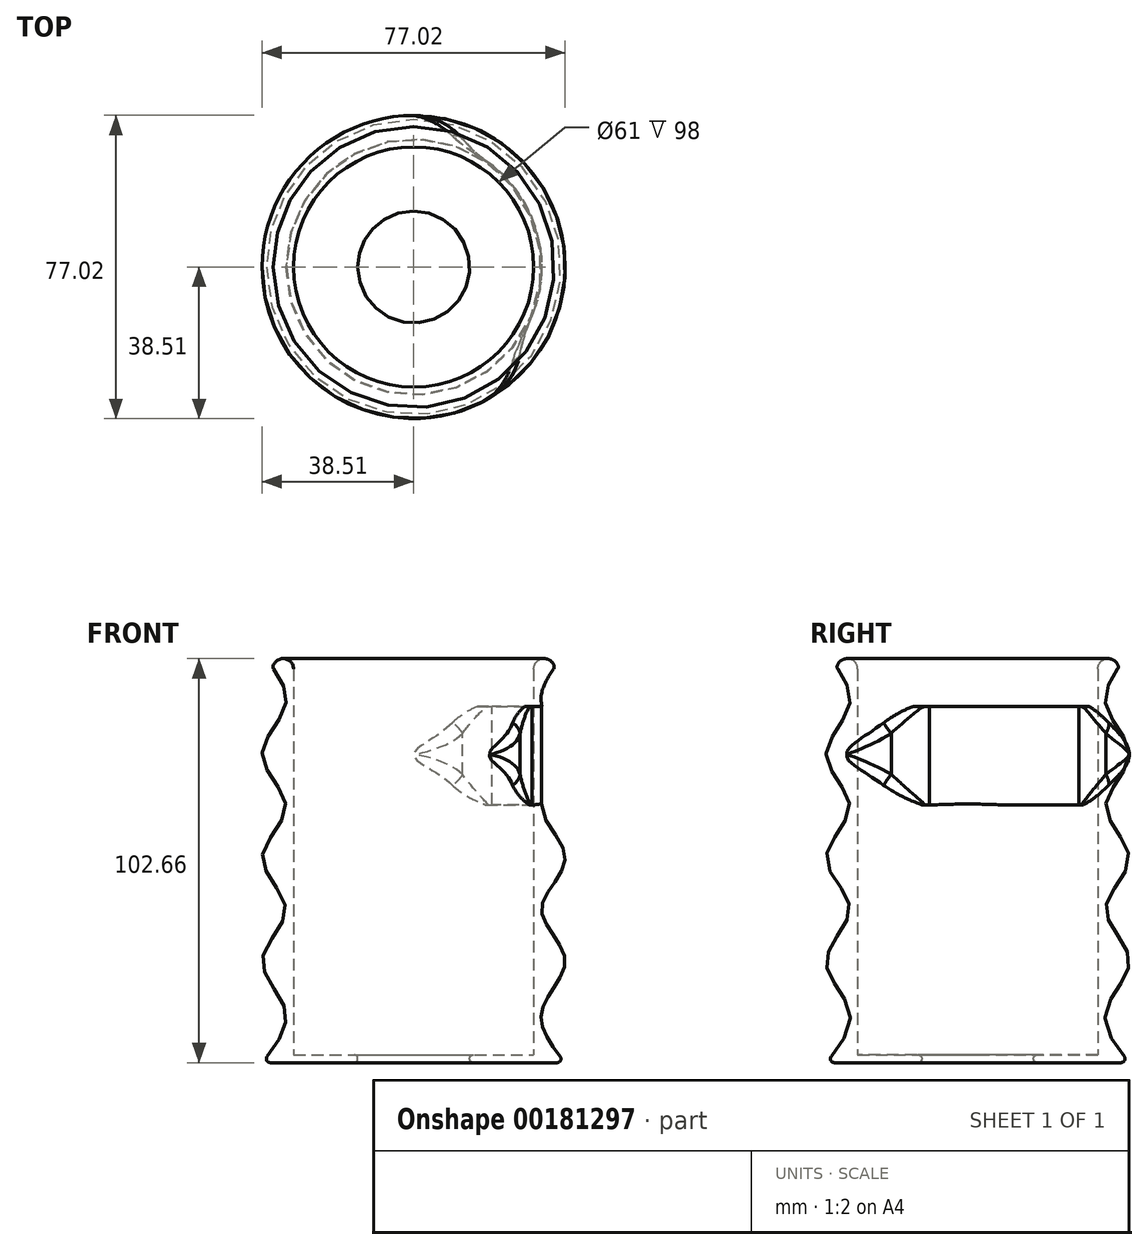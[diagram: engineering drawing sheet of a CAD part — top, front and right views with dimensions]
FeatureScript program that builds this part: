
annotation { "Feature Type Name" : "Feature", "Feature Type Description" : "" }
export const myFeature = defineFeature(function(context is Context, id is Id, definition is map)
    precondition{}
    {
        {
            var Q0;
            Q0=qCreatedBy(makeId("Front.planeOp"),FACE);
            var sketch = newSketch(context, id + "F0", { "sketchPlane" : qUnion([Q0])});
            skLineSegment(sketch, "E0", {"start": v(30.5, 0) * mm, "end": v(30.5, 100) * mm});
            skLineSegment(sketch, "E1", {"start": v(0, 13) * mm, "end": v(106.96, 13) * mm, "construction": true});
            skLineSegment(sketch, "E2.0.1.0", {"start": v(0, 26) * mm, "end": v(106.96, 26) * mm, "construction": true});
            skLineSegment(sketch, "E2.0.2.0", {"start": v(0, 39) * mm, "end": v(106.96, 39) * mm, "construction": true});
            skLineSegment(sketch, "E2.0.3.0", {"start": v(0, 52) * mm, "end": v(106.96, 52) * mm, "construction": true});
            skLineSegment(sketch, "E2.0.4.0", {"start": v(0, 65) * mm, "end": v(106.96, 65) * mm, "construction": true});
            skLineSegment(sketch, "E2.0.5.0", {"start": v(0, 78) * mm, "end": v(106.96, 78) * mm, "construction": true});
            skLineSegment(sketch, "E2.0.6.0", {"start": v(0, 91) * mm, "end": v(106.96, 91) * mm, "construction": true});
            skLineSegment(sketch, "E2.0.7.0", {"start": v(0, 104) * mm, "end": v(106.96, 104) * mm, "construction": true});
            skLineSegment(sketch, "E2.1.0.0", {"start": v(25, 13.02) * mm, "end": v(131.96, 13.02) * mm, "construction": true});
            skLineSegment(sketch, "E2.1.1.0", {"start": v(25, 26.02) * mm, "end": v(131.96, 26.02) * mm, "construction": true});
            skLineSegment(sketch, "E2.1.2.0", {"start": v(25, 39.02) * mm, "end": v(131.96, 39.02) * mm, "construction": true});
            skLineSegment(sketch, "E2.1.3.0", {"start": v(25, 52.02) * mm, "end": v(131.96, 52.02) * mm, "construction": true});
            skLineSegment(sketch, "E2.1.4.0", {"start": v(25, 65.02) * mm, "end": v(131.96, 65.02) * mm, "construction": true});
            skLineSegment(sketch, "E2.1.5.0", {"start": v(25, 78.02) * mm, "end": v(131.96, 78.02) * mm, "construction": true});
            skLineSegment(sketch, "E2.1.6.0", {"start": v(25, 91.02) * mm, "end": v(131.96, 91.02) * mm, "construction": true});
            skLineSegment(sketch, "E2.1.7.0", {"start": v(25, 104.02) * mm, "end": v(131.96, 104.02) * mm, "construction": true});
            skLineSegment(sketch, "E2.2.0.0", {"start": v(50, 13.04) * mm, "end": v(156.96, 13.04) * mm, "construction": true});
            skLineSegment(sketch, "E2.2.1.0", {"start": v(50, 26.04) * mm, "end": v(156.96, 26.04) * mm, "construction": true});
            skLineSegment(sketch, "E2.2.2.0", {"start": v(50, 39.04) * mm, "end": v(156.96, 39.04) * mm, "construction": true});
            skLineSegment(sketch, "E2.2.3.0", {"start": v(50, 52.04) * mm, "end": v(156.96, 52.04) * mm, "construction": true});
            skLineSegment(sketch, "E2.2.4.0", {"start": v(50, 65.04) * mm, "end": v(156.96, 65.04) * mm, "construction": true});
            skLineSegment(sketch, "E2.2.5.0", {"start": v(50, 78.04) * mm, "end": v(156.96, 78.04) * mm, "construction": true});
            skLineSegment(sketch, "E2.2.6.0", {"start": v(50, 91.04) * mm, "end": v(156.96, 91.04) * mm, "construction": true});
            skLineSegment(sketch, "E2.2.7.0", {"start": v(50, 104.04) * mm, "end": v(156.96, 104.04) * mm, "construction": true});
            skLineSegment(sketch, "E2.direction1", {"start": v(0, 13) * mm, "end": v(25, 13.02) * mm, "construction": true});
            skLineSegment(sketch, "E2.direction2", {"start": v(0, 13) * mm, "end": v(0, 26) * mm, "construction": true});
            skLineSegment(sketch, "E3", {"start": v(32.5, 0) * mm, "end": v(32.5, 104) * mm, "construction": true});
            skLineSegment(sketch, "E4", {"start": v(38.5, 0) * mm, "end": v(38.5, 104) * mm, "construction": true});
            skFitSpline(sketch, "E5", {"points": [v(38.5, 0) * mm, v(32.5, 13.02) * mm, v(38.5, 26.02) * mm, v(32.5, 39.02) * mm, v(38.5, 52) * mm, v(32.5, 65.02) * mm, v(38.5, 78.02) * mm, v(32.5, 91.02) * mm, v(38.5, 104) * mm], "startDerivative": vector(-83.13, 104) * mm, "endDerivative": vector(79.18, 106.93) * mm});
            skLineSegment(sketch, "E6", {"start": v(36.43, 0) * mm, "end": v(15.2, 0) * mm});
            skLineSegment(sketch, "E7", {"start": v(30.5, 2) * mm, "end": v(15.2, 2) * mm});
            skArc(sketch, "E8", {"start": v(15.2, 2) * mm, "mid": v(14.2, 1) * mm, "end": v(15.2, 0) * mm});
            skArc(sketch, "E9.filletArc", {"start": v(36.43, 0) * mm, "mid": v(37.33, 0.56) * mm, "end": v(37.22, 1.62) * mm});
            skLineSegment(sketch, "E10", {"start": v(0, 0) * mm, "end": v(0, 131.89) * mm, "construction": true});
            skArc(sketch, "E11", {"start": v(30.5, 100) * mm, "mid": v(32.7, 102.62) * mm, "end": v(35.65, 100.9) * mm});
            skPoint(sketch, "E12.visualSharp", {"position": v(35.79, 100.34) * mm});
            skArc(sketch, "E12.filletArc", {"start": v(35.53, 99.97) * mm, "mid": v(35.7, 100.42) * mm, "end": v(35.65, 100.9) * mm});
            skSolve(sketch);
        }
        {
            var Q0;
            Q0=qSketchRegion(id+"F0",true);
            var Q1;
            Q1=sQuery(id+"F0.wireOp",EDGE,"E10");
            revolve(context, id + "F1", {"entities" : qUnion([Q0]), "axis" : qUnion([Q1]), "revolveType" : RevolveType.FULL});
        }
        {
            var Q0;
            Q0=qCreatedBy(makeId("Top.planeOp"),FACE);
            cPlane(context, id + "F2", {"entities" : qUnion([Q0]), "cplaneType" : CPlaneType.OFFSET, "offset" : 78.04 * mm, "width" : 150 * mm, "height" : 150 * mm});
        }
        {
            var Q0;
            Q0=qCreatedBy(id+"F2.planeOp",FACE);
            var sketch = newSketch(context, id + "F3", { "sketchPlane" : qUnion([Q0])});
            skCircle(sketch, "E13.0", {"center": v(0, 0) * mm, "radius": 30.5 * mm});
            skCircle(sketch, "E14.0", {"center": v(0, 0) * mm, "radius": 30.5 * mm, "construction": true});
            skArc(sketch, "E15.0", {"start": v(0, 32.51) * mm, "mid": v(-32.5, 0.01) * mm, "end": v(0, -32.49) * mm, "construction": true});
            skArc(sketch, "E16.0", {"start": v(0, 38.51) * mm, "mid": v(-38.5, 0.01) * mm, "end": v(0, -38.49) * mm, "construction": true});
            skLineSegment(sketch, "E17", {"start": v(0, 0) * mm, "end": v(0.18, 0) * mm, "construction": true});
            skLineSegment(sketch, "E18", {"start": v(0, 52.86) * mm, "end": v(0, -52.45) * mm, "construction": true});
            skArc(sketch, "E19.trimOffspring", {"start": v(38.5, 0) * mm, "mid": v(35.57, 14.74) * mm, "end": v(27.23, 27.23) * mm, "construction": true});
            skArc(sketch, "E20.0", {"start": v(25.21, 25.21) * mm, "mid": v(35.36, -4.58) * mm, "end": v(17.96, -30.8) * mm, "construction": true});
            skLineSegment(sketch, "E21", {"start": v(0.18, 0) * mm, "end": v(32.1, -55.28) * mm, "construction": true});
            skPoint(sketch, "E22.start.orphan", {"position": v(12.45, 32.51) * mm});
            skPoint(sketch, "E23.orphan", {"position": v(22.98, -22.98) * mm});
            skPoint(sketch, "E24.MirrorCS.start.orphan", {"position": v(12.45, -32.51) * mm});
            skPoint(sketch, "E25.orphan", {"position": v(0, -38.51) * mm});
            skArc(sketch, "E26.trimOffspring", {"start": v(0, -35.65) * mm, "mid": v(-35.65, 0) * mm, "end": v(0, 35.65) * mm, "construction": true});
            skPoint(sketch, "E27.end.orphan", {"position": v(22.98, 22.98) * mm});
            skLineSegment(sketch, "E28.trimOffspring", {"start": v(30.5, 0) * mm, "end": v(38.5, 0) * mm, "construction": true});
            skLineSegment(sketch, "E29", {"start": v(0, 0) * mm, "end": v(80.6, 21.6) * mm, "construction": true});
            skLineSegment(sketch, "E30", {"start": v(0.18, 0) * mm, "end": v(49.88, 64.77) * mm, "construction": true});
            skLineSegment(sketch, "E31", {"start": v(0.18, 0) * mm, "end": v(81.97, -33.88) * mm, "construction": true});
            skArc(sketch, "E32", {"start": v(0, 32.51) * mm, "mid": v(32.5, 0.01) * mm, "end": v(0, -32.49) * mm, "construction": true});
            skArc(sketch, "E33", {"start": v(31.4, 8.41) * mm, "mid": v(27, 17.96) * mm, "end": v(19.9, 25.7) * mm});
            skArc(sketch, "E34", {"start": v(12.45, 32.51) * mm, "mid": v(6.87, 36.85) * mm, "end": v(0, 38.51) * mm});
            skArc(sketch, "E35", {"start": v(12.45, 32.51) * mm, "mid": v(15.98, 28.9) * mm, "end": v(19.9, 25.7) * mm});
            skArc(sketch, "E36.MirrorCS", {"start": v(27.04, -21.93) * mm, "mid": v(24.38, -28.48) * mm, "end": v(19.26, -33.35) * mm});
            skArc(sketch, "E37.MirrorCS", {"start": v(27.04, -21.93) * mm, "mid": v(28.29, -17.03) * mm, "end": v(30.09, -12.3) * mm});
            skArc(sketch, "E38", {"start": v(30.09, -12.3) * mm, "mid": v(32.47, -2.06) * mm, "end": v(31.4, 8.41) * mm});
            skArc(sketch, "E39", {"start": v(19.26, -33.35) * mm, "mid": v(38.75, 10.38) * mm, "end": v(0, 38.51) * mm});
            skSolve(sketch);
        }
        {
            var Q0;
            Q0=qSketchRegion(id+"F3",true);
            extrude(context, id + "F4", {"entities" : qUnion([Q0]), "operationType" : NewBodyOperationType.REMOVE, "endBound" : BoundingType.SYMMETRIC, "oppositeDirection" : true, "depth" : 25 * mm});
        }
        {
            var Q0;
            Q0=makeQuery(id+"F4.boolean.opBoolean","INTERSECT",EDGE,{"disambiguationData":[OD(0.0)],"derivedFrom":[makeQuery(id+"F1.opRevolve","SWEPT_FACE",FACE,{"disambiguationData":[OSD([sQuery(id+"F0.wireOp",EDGE,"E5")])]}),makeQuery(id+"F4.opExtrude","SWEPT_FACE",FACE,{"disambiguationData":[OSD([sQuery(id+"F3.wireOp",EDGE,"E35")])]})]});
            var Q1;
            Q1=makeQuery(id+"F4.boolean.opBoolean","INTERSECT",EDGE,{"derivedFrom":[makeQuery(id+"F1.opRevolve","SWEPT_FACE",FACE,{"disambiguationData":[OSD([sQuery(id+"F0.wireOp",EDGE,"E5")])]}),makeQuery(id+"F4.opExtrude","SWEPT_FACE",FACE,{"disambiguationData":[OSD([sQuery(id+"F3.wireOp",EDGE,"E34")])]})]});
            var Q2;
            Q2=makeQuery(id+"F4.boolean.opBoolean","INTERSECT",EDGE,{"disambiguationData":[OD(1.0)],"derivedFrom":[makeQuery(id+"F1.opRevolve","SWEPT_FACE",FACE,{"disambiguationData":[OSD([sQuery(id+"F0.wireOp",EDGE,"E5")])]}),makeQuery(id+"F4.opExtrude","SWEPT_FACE",FACE,{"disambiguationData":[OSD([sQuery(id+"F3.wireOp",EDGE,"E35")])]})]});
            var Q3;
            Q3=makeQuery(id+"F4.boolean.opBoolean","INTERSECT",EDGE,{"disambiguationData":[OD(1.0)],"derivedFrom":[makeQuery(id+"F1.opRevolve","SWEPT_FACE",FACE,{"disambiguationData":[OSD([sQuery(id+"F0.wireOp",EDGE,"E5")])]}),makeQuery(id+"F4.opExtrude","SWEPT_FACE",FACE,{"disambiguationData":[OSD([sQuery(id+"F3.wireOp",EDGE,"E37.MirrorCS")])]})]});
            var Q4;
            Q4=makeQuery(id+"F4.boolean.opBoolean","INTERSECT",EDGE,{"derivedFrom":[makeQuery(id+"F1.opRevolve","SWEPT_FACE",FACE,{"disambiguationData":[OSD([sQuery(id+"F0.wireOp",EDGE,"E5")])]}),makeQuery(id+"F4.opExtrude","SWEPT_FACE",FACE,{"disambiguationData":[OSD([sQuery(id+"F3.wireOp",EDGE,"E36.MirrorCS")])]})]});
            var Q5;
            Q5=makeQuery(id+"F4.boolean.opBoolean","INTERSECT",EDGE,{"disambiguationData":[OD(0.0)],"derivedFrom":[makeQuery(id+"F1.opRevolve","SWEPT_FACE",FACE,{"disambiguationData":[OSD([sQuery(id+"F0.wireOp",EDGE,"E5")])]}),makeQuery(id+"F4.opExtrude","SWEPT_FACE",FACE,{"disambiguationData":[OSD([sQuery(id+"F3.wireOp",EDGE,"E37.MirrorCS")])]})]});
            fillet(context, id + "F5", {"entities" : qUnion([Q0, Q1, Q2, Q3, Q4, Q5]), "radius" : 5 * mm, "tangentPropagation" : true, "allowEdgeOverflow" : false});
        }
    });
